# Revit family: Deca_Cuba de Sobrepor Redonda_L
name_source: partatom
category: Plumbing Fixtures
revit_build: Autodesk Revit Architecture 2012 (Build: 20110916_2132(x64)
units: mm (PartAtom-declared; Revit-internal decimal feet)

## types (1)
- L.1050.17_Branco Gelo GE17
    Aprovado por = Contino/quattroD
    Assembly Code = D2010400
    Atendimento ao Cliente = 0800-0117073
    Criado por = Contino/quattroD
    Cuba = Deca GE17 Branco Gelo Cerâmica
    Código = L.1050.17
    Default Elevation = 0 mm  [stored 0 ft]
    Description = Cuba de sobrepor
    Diâmetro Ponto de Esgoto = 40 mm  [stored 0.131234 ft]
    Flow Pressure = 0.00 psi
    Linha = Cuba de sobrepor
    Louça/Metais = Louça
    Manufacturer = Deca
    Material = Deca_Vitreous China
    Model = L.1050.17
    Norma = ABNT NBR 15097-1: 2011 / ABNT NBR 15097-2: 2011
    Peso Liquido (Kg) = 8.14
    Produto = Cuba de sobrepor redonda
    Raio Ponto de Esgoto = 20 mm  [stored 0.0656168 ft]
    Segmento = Luxo
    URL = www.deca.com.br/produtos
    Variações de COR = Branco (L.1050.17)
    Vendido Separadamente = Sifão para lavatório: Cromado: (1680.C.100.112), Dourado (1680.D.100.112).   Slim: Cromado (1684.C.100.112), Dourado (1684.D.100.112) e Gold (1684.D.100.112.GLD).  Quadra: Cromado (1685.C.100.112).                                                                                                                                                                                                                                                                                                                                                                                                                                                                                                  Válvulas de escoamentos compatíveis: Luxo: Cromado (1601.C), Branco (1601.E.BR), Gold (1601.D.GLD); Click: Cromado (1601.C.CLI).  Competitivo: Cromado (1602.C), Dourado (1602.D); Tampão plástico: Cromado (1602.C.PLA).
    WFU = 0

note: [stored X ft] marks values corroborated as IEEE doubles in the binary element streams (Revit-internal decimal feet)

## geometry (parser evidence)
native form markers: Blend x4, Sweep x2
no freeform markers — native parametric forms only
